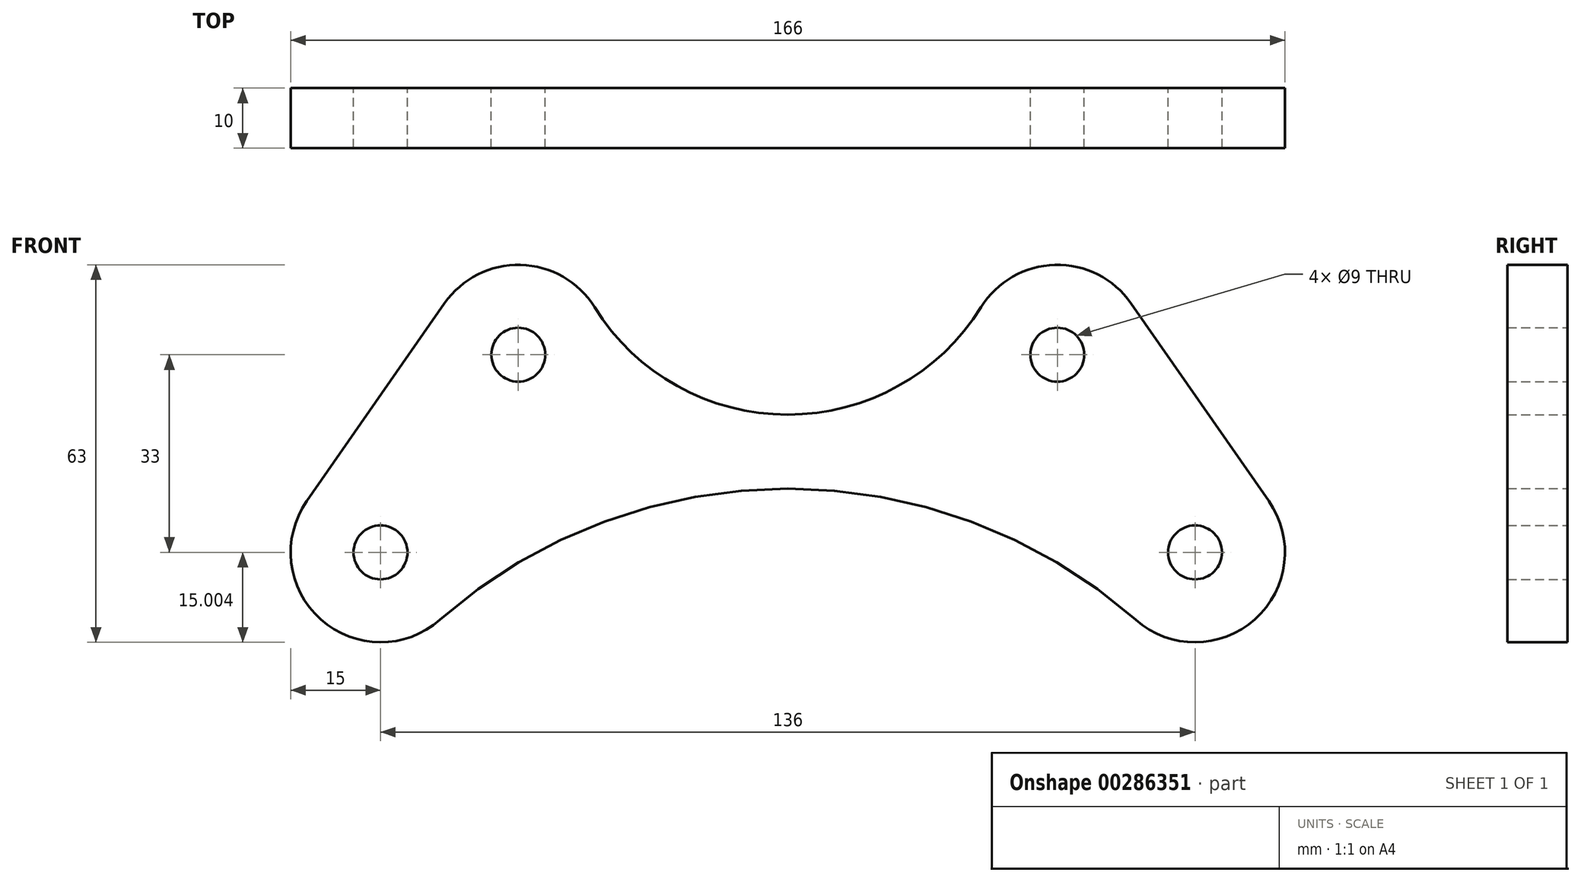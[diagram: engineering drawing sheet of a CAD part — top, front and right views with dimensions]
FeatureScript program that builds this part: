
annotation { "Feature Type Name" : "Feature", "Feature Type Description" : "" }
export const myFeature = defineFeature(function(context is Context, id is Id, definition is map)
    precondition{}
    {
        {
            var Q0;
            Q0=qCreatedBy(makeId("Front.planeOp"),FACE);
            var sketch = newSketch(context, id + "F0", { "sketchPlane" : qUnion([Q0])});
            skCircle(sketch, "E0", {"center": v(-68, 73.7) * mm, "radius": 4.5 * mm});
            skCircle(sketch, "E1", {"center": v(68, 73.7) * mm, "radius": 4.5 * mm});
            skCircle(sketch, "E2", {"center": v(-45, 106.7) * mm, "radius": 4.5 * mm});
            skCircle(sketch, "E3", {"center": v(45, 106.7) * mm, "radius": 4.5 * mm});
            skArc(sketch, "E4", {"start": v(-32.26, 114.63) * mm, "mid": v(0, 96.7) * mm, "end": v(32.26, 114.63) * mm});
            skLineSegment(sketch, "E5", {"start": v(-57.3, 115.28) * mm, "end": v(-80.3, 82.28) * mm});
            skLineSegment(sketch, "E6", {"start": v(57.3, 115.28) * mm, "end": v(80.3, 82.28) * mm});
            skArc(sketch, "E7", {"start": v(-32.26, 114.63) * mm, "mid": v(-44.6, 121.7) * mm, "end": v(-57.3, 115.28) * mm});
            skArc(sketch, "E8", {"start": v(57.3, 115.28) * mm, "mid": v(44.6, 121.7) * mm, "end": v(32.26, 114.63) * mm});
            skArc(sketch, "E9", {"start": v(-80.3, 82.28) * mm, "mid": v(-78, 62.52) * mm, "end": v(-58.1, 62.44) * mm});
            skArc(sketch, "E10", {"start": v(58.1, 62.44) * mm, "mid": v(78, 62.52) * mm, "end": v(80.3, 82.28) * mm});
            skCircle(sketch, "E11", {"center": v(0, 0) * mm, "radius": 115.8 * mm, "construction": true});
            skArc(sketch, "E12", {"start": v(58.1, 62.44) * mm, "mid": v(0, 84.34) * mm, "end": v(-58.1, 62.44) * mm});
            skSolve(sketch);
        }
        {
            var Q0;
            Q0 = qSketchRegion(id + "F0", true);
            extrude(context, id + "F1", {"entities" : qUnion([Q0]), "depth" : 10 * mm});
        }
    });
